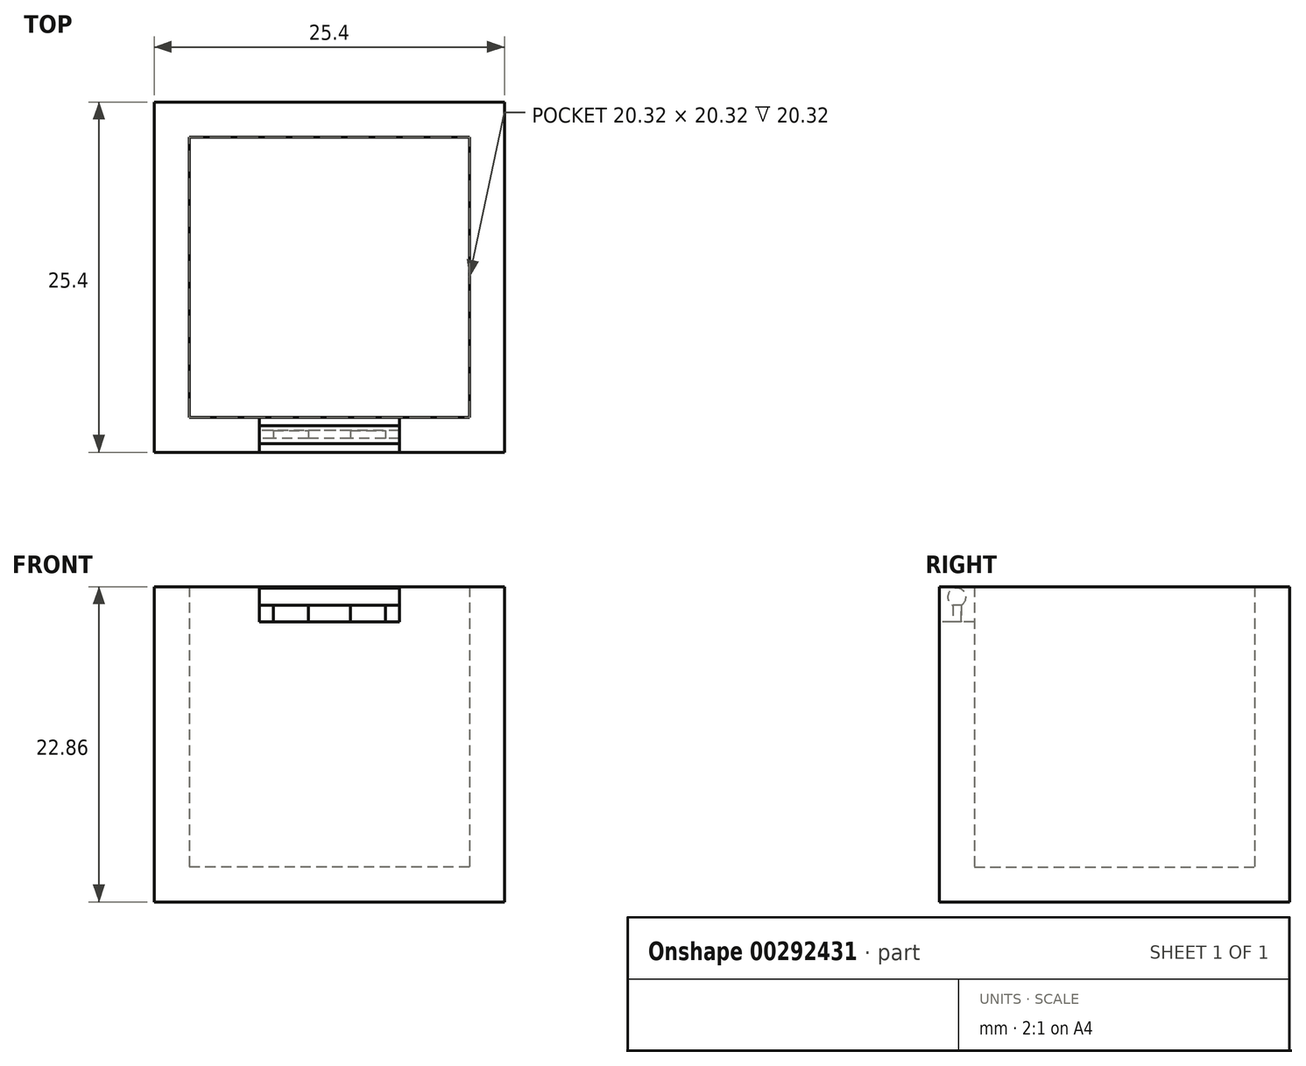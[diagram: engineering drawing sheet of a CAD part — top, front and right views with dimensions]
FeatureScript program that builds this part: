
annotation { "Feature Type Name" : "Feature", "Feature Type Description" : "" }
export const myFeature = defineFeature(function(context is Context, id is Id, definition is map)
    precondition{}
    {
        {
            var Q0;
            Q0=qCreatedBy(makeId("Top.planeOp"),FACE);
            var sketch = newSketch(context, id + "F0", { "sketchPlane" : qUnion([Q0])});
            skLineSegment(sketch, "E0.bottom", {"start": v(-12.33, 11.82) * mm, "end": v(13.07, 11.82) * mm});
            skLineSegment(sketch, "E0.top", {"start": v(-12.33, -13.58) * mm, "end": v(13.07, -13.58) * mm});
            skLineSegment(sketch, "E0.left", {"start": v(-12.33, 11.82) * mm, "end": v(-12.33, -13.58) * mm});
            skLineSegment(sketch, "E0.right", {"start": v(13.07, 11.82) * mm, "end": v(13.07, -13.58) * mm});
            skLineSegment(sketch, "E1.bottom", {"start": v(-9.79, 9.28) * mm, "end": v(10.53, 9.28) * mm});
            skLineSegment(sketch, "E1.top", {"start": v(-9.79, -11.04) * mm, "end": v(10.53, -11.04) * mm});
            skLineSegment(sketch, "E1.left", {"start": v(-9.79, 9.28) * mm, "end": v(-9.79, -11.04) * mm});
            skLineSegment(sketch, "E1.right", {"start": v(10.53, 9.28) * mm, "end": v(10.53, -11.04) * mm});
            skSolve(sketch);
        }
        {
            var Q0;
            Q0=makeQuery(id+"F0.imprint","IMPRINT",FACE,{"disambiguationData":[TD([[makeQuery(id+"F0.imprint","IMPRINT",EDGE,{"derivedFrom":sQuery(id+"F0.wireOp",EDGE,"E1.bottom")}),-1.0]])]});
            var Q1;
            Q1=makeQuery(id+"F0.imprint","IMPRINT",FACE,{"disambiguationData":[TD([[makeQuery(id+"F0.imprint","IMPRINT",EDGE,{"derivedFrom":sQuery(id+"F0.wireOp",EDGE,"E0.bottom")}),-1.0]])]});
            extrude(context, id + "F1", {"entities" : qUnion([Q0, Q1]), "depth" : 2.54 * mm});
        }
        {
            var Q0;
            Q0=qSketchRegion(id+"F0",true);
            extrude(context, id + "F2", {"entities" : qUnion([Q0]), "operationType" : NewBodyOperationType.ADD, "depth" : 22.86 * mm});
        }
        {
            var Q0;
            {var subQ0=sQuery(id+"F0.wireOp",EDGE,"E0.top");Q0=makeQuery(id+"F2.boolean.opBoolean","MERGE",FACE,{"derivedFrom":[makeQuery(id+"F1.opExtrude","SWEPT_FACE",FACE,{"disambiguationData":[OSD([subQ0])]}),makeQuery(id+"F2.opExtrude","SWEPT_FACE",FACE,{"disambiguationData":[OSD([subQ0])]})]});}
            var sketch = newSketch(context, id + "F3", { "sketchPlane" : qUnion([Q0])});
            skLineSegment(sketch, "E2", {"start": v(-4.7, 22.86) * mm, "end": v(-4.7, 20.32) * mm});
            skLineSegment(sketch, "E3", {"start": v(-4.7, 20.32) * mm, "end": v(5.45, 20.32) * mm});
            skLineSegment(sketch, "E4", {"start": v(5.45, 20.32) * mm, "end": v(5.45, 22.86) * mm});
            skLineSegment(sketch, "E5", {"start": v(-4.7, 22.86) * mm, "end": v(5.45, 22.86) * mm});
            skSolve(sketch);
        }
        {
            var Q0;
            Q0=makeQuery(id+"F3.imprint","IMPRINT",FACE,{"disambiguationData":[TD([[makeQuery(id+"F3.imprint","IMPRINT",EDGE,{"derivedFrom":sQuery(id+"F3.wireOp",EDGE,"E2")}),1.0]])]});
            extrude(context, id + "F4", {"entities" : qUnion([Q0]), "operationType" : NewBodyOperationType.REMOVE, "oppositeDirection" : true, "depth" : 2.54 * mm});
        }
        {
            var Q0;
            Q0=makeQuery(id+"F4.boolean.opBoolean","COPY",FACE,{"derivedFrom":makeQuery(id+"F4.opExtrude","SWEPT_FACE",FACE,{"disambiguationData":[OSD([sQuery(id+"F3.wireOp",EDGE,"E2")])]})});
            var sketch = newSketch(context, id + "F5", { "sketchPlane" : qUnion([Q0])});
            skCircle(sketch, "E6", {"center": v(-12.31, 22.1) * mm, "radius": 0.66 * mm});
            skPoint(sketch, "E6.centerSnap0", {"position": v(-13.58, 22.1) * mm});
            skPoint(sketch, "E6.centerSnap1", {"position": v(-12.31, 22.86) * mm});
            skLineSegment(sketch, "E7.left", {"start": v(-12.6, 21.5) * mm, "end": v(-12.6, 21.5) * mm});
            skLineSegment(sketch, "E7.right", {"start": v(-12, 21.48) * mm, "end": v(-12, 21.52) * mm});
            skLineSegment(sketch, "E8.top", {"start": v(-12.6, 20.32) * mm, "end": v(-12, 20.32) * mm});
            skLineSegment(sketch, "E8.left", {"start": v(-12.6, 21.5) * mm, "end": v(-12.6, 20.32) * mm});
            skLineSegment(sketch, "E8.right", {"start": v(-12, 21.52) * mm, "end": v(-12, 20.32) * mm});
            skSolve(sketch);
        }
        {
            var Q0;
            Q0=makeQuery(id+"F5.imprint","IMPRINT",FACE,{"disambiguationData":[TD([[makeQuery(id+"F5.imprint","IMPRINT",EDGE,{"derivedFrom":sQuery(id+"F5.wireOp",EDGE,"E6")}),1.0]])]});
            var Q1;
            {var subQ5=sQuery(id+"F5.wireOp",EDGE,"E8.top");Q1=makeQuery(id+"F5.imprint","IMPRINT",FACE,{"disambiguationData":[TD([[makeQuery(id+"F5.imprint","IMPRINT",EDGE,{"derivedFrom":subQ5}),-1.0]])]});}
            extrude(context, id + "F6", {"entities" : qUnion([Q0, Q1]), "operationType" : NewBodyOperationType.ADD, "depth" : 10.16 * mm});
        }
        {
            var Q0;
            Q0=makeQuery(id+"F6.opExtrude","SWEPT_FACE",FACE,{"disambiguationData":[OSD([sQuery(id+"F5.wireOp",EDGE,"E7.left"),sQuery(id+"F5.wireOp",EDGE,"E8.left")])]});
            var sketch = newSketch(context, id + "F7", { "sketchPlane" : qUnion([Q0])});
            skLineSegment(sketch, "E9.bottom", {"start": v(-3.7, 21.5) * mm, "end": v(-1.15, 21.5) * mm});
            skLineSegment(sketch, "E9.top", {"start": v(-3.7, 20.32) * mm, "end": v(-1.15, 20.32) * mm});
            skLineSegment(sketch, "E9.left", {"start": v(-3.7, 21.5) * mm, "end": v(-3.7, 20.32) * mm});
            skLineSegment(sketch, "E9.right", {"start": v(-1.15, 21.5) * mm, "end": v(-1.15, 20.32) * mm});
            skLineSegment(sketch, "E10.bottom", {"start": v(1.9, 21.5) * mm, "end": v(4.44, 21.5) * mm});
            skLineSegment(sketch, "E10.top", {"start": v(1.9, 20.32) * mm, "end": v(4.44, 20.32) * mm});
            skLineSegment(sketch, "E10.left", {"start": v(1.9, 21.5) * mm, "end": v(1.9, 20.32) * mm});
            skLineSegment(sketch, "E10.right", {"start": v(4.44, 21.5) * mm, "end": v(4.44, 20.32) * mm});
            skSolve(sketch);
        }
        {
            var Q0;
            Q0=makeQuery(id+"F7.imprint","IMPRINT",FACE,{"disambiguationData":[TD([[makeQuery(id+"F7.imprint","IMPRINT",EDGE,{"derivedFrom":sQuery(id+"F7.wireOp",EDGE,"E9.bottom")}),1.0]])]});
            var Q1;
            Q1=makeQuery(id+"F7.imprint","IMPRINT",FACE,{"disambiguationData":[TD([[makeQuery(id+"F7.imprint","IMPRINT",EDGE,{"derivedFrom":sQuery(id+"F7.wireOp",EDGE,"E10.bottom")}),1.0]])]});
            extrude(context, id + "F8", {"entities" : qUnion([Q0, Q1]), "operationType" : NewBodyOperationType.REMOVE, "oppositeDirection" : true, "depth" : 2.54 * mm});
        }
    });
